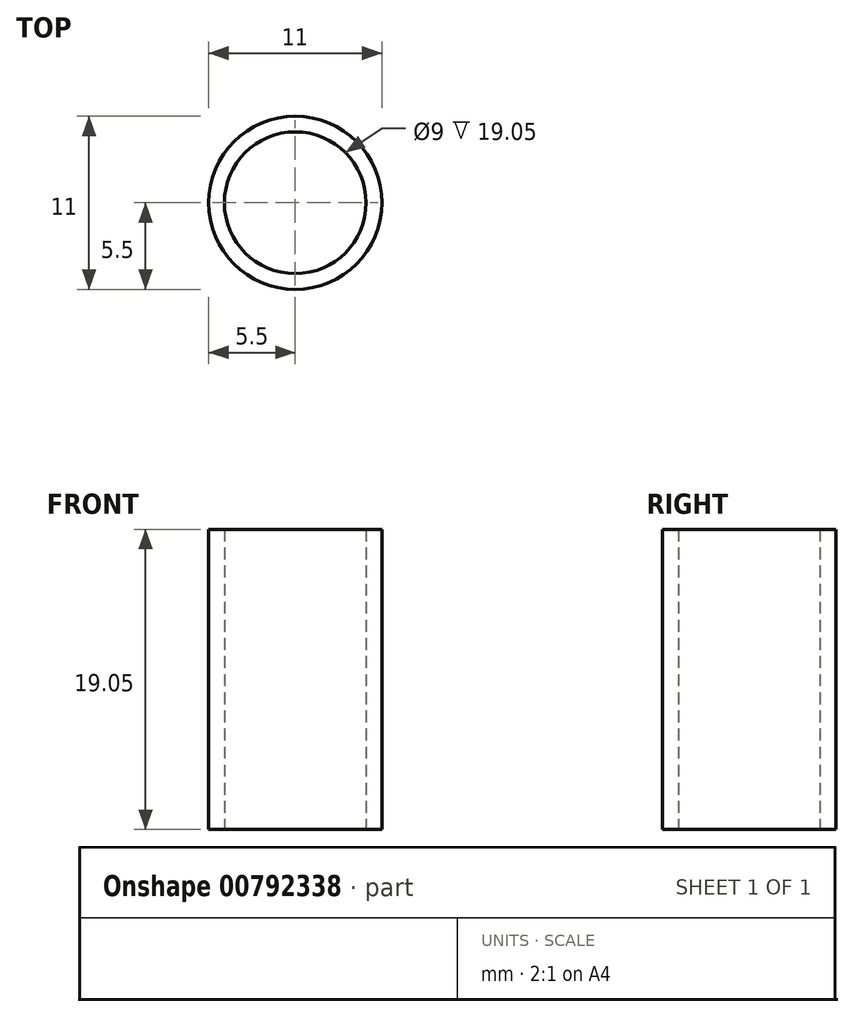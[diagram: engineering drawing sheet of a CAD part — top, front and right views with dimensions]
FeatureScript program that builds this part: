
annotation { "Feature Type Name" : "Feature", "Feature Type Description" : "" }
export const myFeature = defineFeature(function(context is Context, id is Id, definition is map)
    precondition{}
    {
        {
            var Q0;
            Q0=qCreatedBy(makeId("Top.planeOp"),FACE);
            var sketch = newSketch(context, id + "F0", { "sketchPlane" : qUnion([Q0])});
            skCircle(sketch, "E0", {"center": v(0, 0) * mm, "radius": 5.5 * mm});
            skSolve(sketch);
        }
        {
            var Q0;
            Q0=makeQuery(id+"F0.imprint","IMPRINT",FACE,{"disambiguationData":[TD([[makeQuery(id+"F0.imprint","IMPRINT",EDGE,{"derivedFrom":sQuery(id+"F0.wireOp",EDGE,"E0")}),1.0]])]});
            var Q1;
            Q1=sQuery(id+"F0.wireOp",EDGE,"E0");
            extrude(context, id + "F1", {"entities" : qUnion([Q0]), "surfaceEntities" : qUnion([Q1]), "depth" : 19.05 * mm, "offsetDistance" : 25.4 * mm});
        }
        {
            var Q0;
            Q0=qCreatedBy(makeId("Top.planeOp"),FACE);
            var sketch = newSketch(context, id + "F2", { "sketchPlane" : qUnion([Q0])});
            skCircle(sketch, "E1", {"center": v(0, 0) * mm, "radius": 4.5 * mm});
            skSolve(sketch);
        }
        {
            var Q0;
            Q0=makeQuery(id+"F2.imprint","IMPRINT",FACE,{"disambiguationData":[TD([[makeQuery(id+"F2.imprint","IMPRINT",EDGE,{"derivedFrom":sQuery(id+"F2.wireOp",EDGE,"E1")}),1.0]])]});
            extrude(context, id + "F3", {"entities" : qUnion([Q0]), "operationType" : NewBodyOperationType.REMOVE, "depth" : 76.7 * mm, "offsetDistance" : 25.4 * mm});
        }
    });
